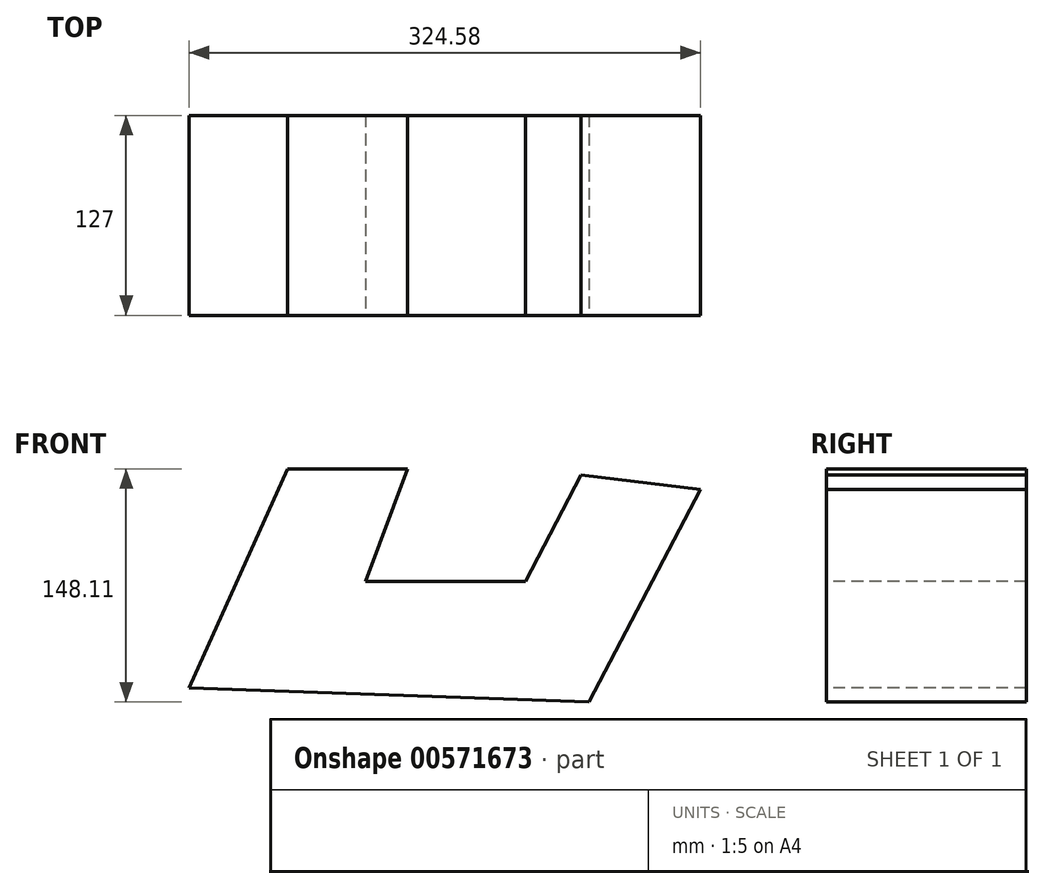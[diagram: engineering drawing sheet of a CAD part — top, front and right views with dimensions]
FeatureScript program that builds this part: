
annotation { "Feature Type Name" : "Feature", "Feature Type Description" : "" }
export const myFeature = defineFeature(function(context is Context, id is Id, definition is map)
    precondition{}
    {
        {
            var Q0;
            Q0=qCreatedBy(makeId("Front.planeOp"),FACE);
            var sketch = newSketch(context, id + "F0", { "sketchPlane" : qUnion([Q0])});
            skLineSegment(sketch, "E0", {"start": v(0, 0) * mm, "end": v(62.36, 139.06) * mm});
            skLineSegment(sketch, "E1", {"start": v(62.36, 139.06) * mm, "end": v(138.56, 139.06) * mm});
            skLineSegment(sketch, "E2", {"start": v(138.56, 139.06) * mm, "end": v(112.07, 67.6) * mm});
            skLineSegment(sketch, "E3", {"start": v(112.07, 67.6) * mm, "end": v(213.67, 67.6) * mm});
            skLineSegment(sketch, "E4", {"start": v(213.67, 67.6) * mm, "end": v(248.94, 135.16) * mm});
            skLineSegment(sketch, "E5", {"start": v(248.94, 135.16) * mm, "end": v(324.58, 125.94) * mm});
            skLineSegment(sketch, "E6", {"start": v(324.58, 125.94) * mm, "end": v(253.84, -9.05) * mm});
            skLineSegment(sketch, "E7", {"start": v(253.84, -9.05) * mm, "end": v(0, 0) * mm});
            skSolve(sketch);
        }
        {
            var Q0;
            Q0 = qSketchRegion(id + "F0", true);
            extrude(context, id + "F1", {"entities" : qUnion([Q0]), "oppositeDirection" : true, "depth" : 127 * mm, "offsetDistance" : 25.4 * mm});
        }
    });
